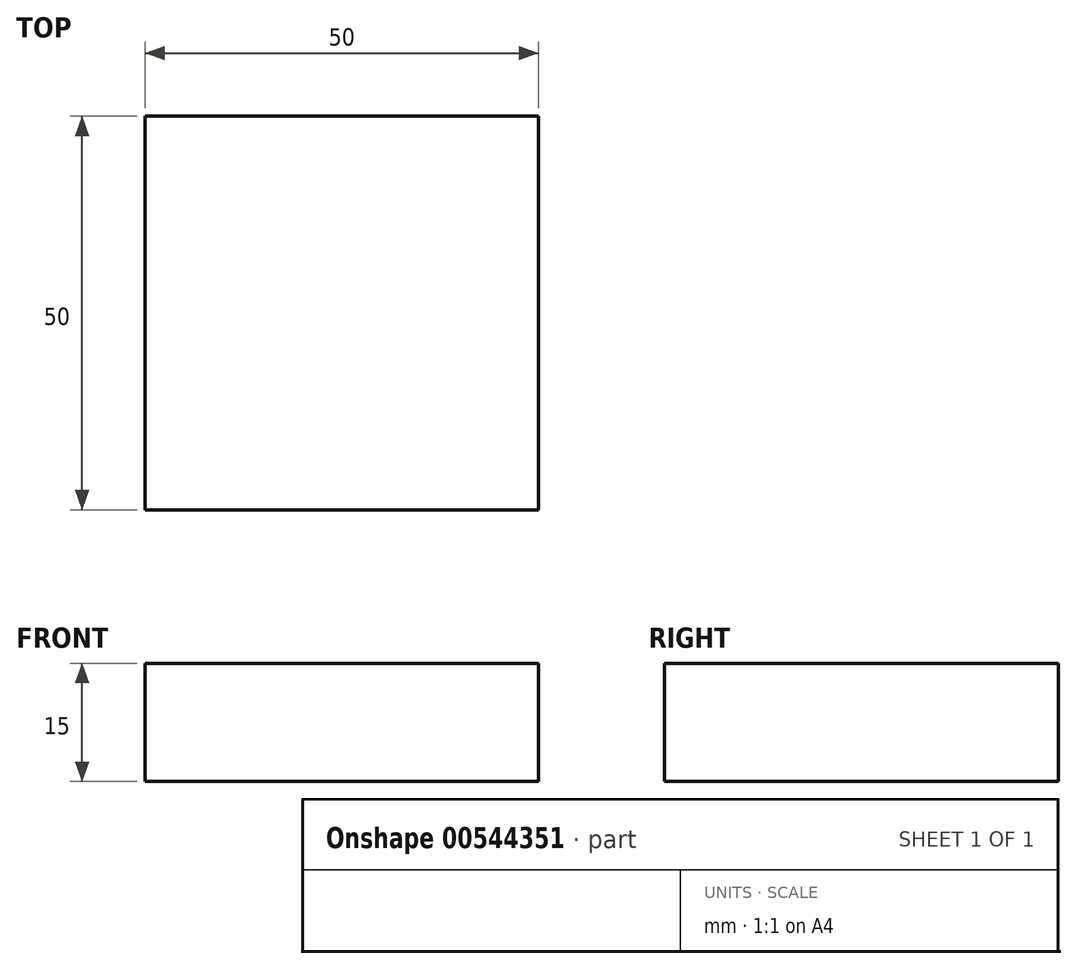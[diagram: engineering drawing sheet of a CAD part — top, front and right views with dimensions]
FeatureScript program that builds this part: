
annotation { "Feature Type Name" : "Feature", "Feature Type Description" : "" }
export const myFeature = defineFeature(function(context is Context, id is Id, definition is map)
    precondition{}
    {
        {
            var Q0;
            Q0=qCreatedBy(makeId("Top.planeOp"),FACE);
            var sketch = newSketch(context, id + "F0", { "sketchPlane" : qUnion([Q0])});
            skLineSegment(sketch, "E0.bottom", {"start": v(0, 0) * mm, "end": v(50, 0) * mm});
            skLineSegment(sketch, "E0.top", {"start": v(0, 50) * mm, "end": v(50, 50) * mm});
            skLineSegment(sketch, "E0.left", {"start": v(0, 0) * mm, "end": v(0, 50) * mm});
            skLineSegment(sketch, "E0.right", {"start": v(50, 0) * mm, "end": v(50, 50) * mm});
            skSolve(sketch);
        }
        {
            var Q0;
            Q0=makeQuery(id+"F0.imprint","IMPRINT",FACE,{"disambiguationData":[TD([[makeQuery(id+"F0.imprint","IMPRINT",EDGE,{"derivedFrom":sQuery(id+"F0.wireOp",EDGE,"E0.bottom")}),1.0]])]});
            extrude(context, id + "F1", {"entities" : qUnion([Q0]), "depth" : 15 * mm, "offsetDistance" : 25 * mm});
        }
    });
